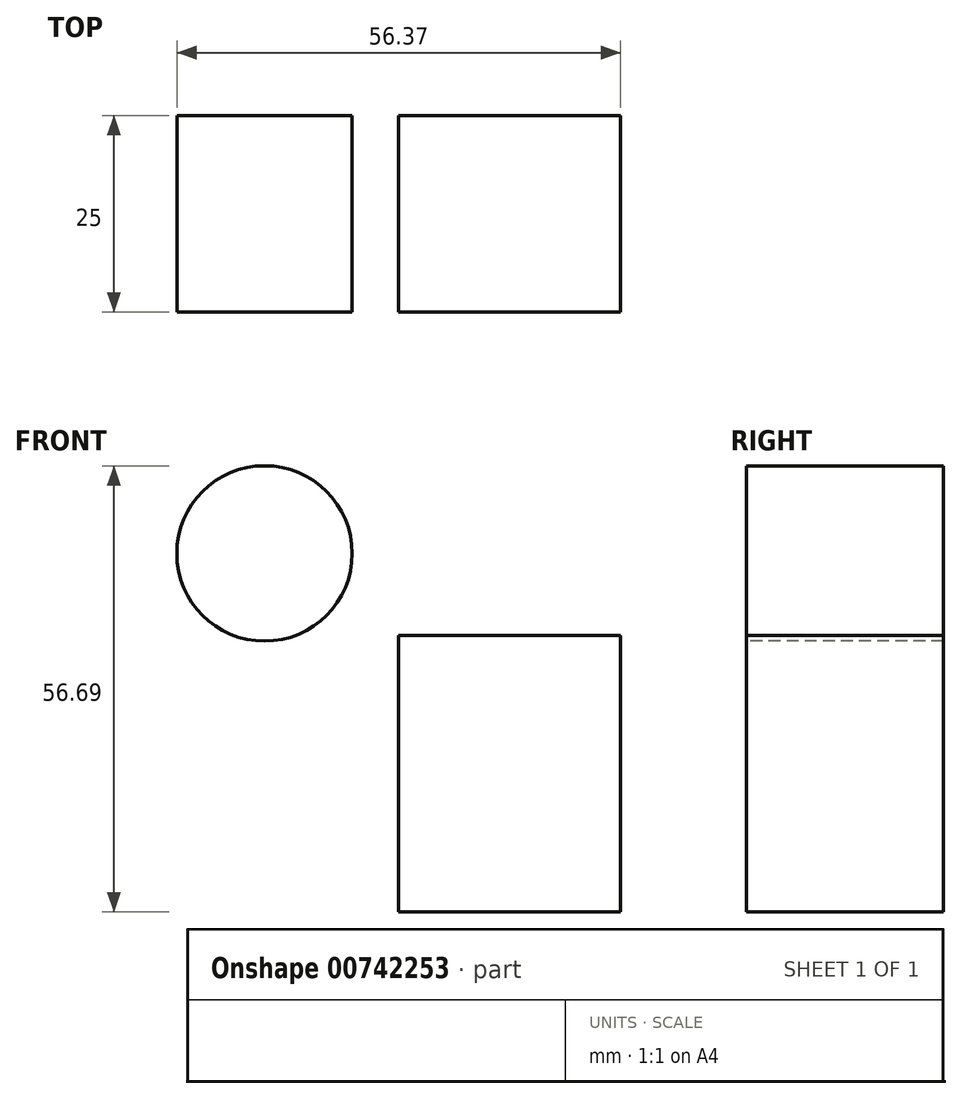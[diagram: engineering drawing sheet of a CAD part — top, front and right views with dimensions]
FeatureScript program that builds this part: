
annotation { "Feature Type Name" : "Feature", "Feature Type Description" : "" }
export const myFeature = defineFeature(function(context is Context, id is Id, definition is map)
    precondition{}
    {
        {
            var Q0;
            Q0=qCreatedBy(makeId("Front.planeOp"),FACE);
            var sketch = newSketch(context, id + "F0", { "sketchPlane" : qUnion([Q0])});
            skLineSegment(sketch, "E0.bottom", {"start": v(34.98, 28.17) * mm, "end": v(63.2, 28.17) * mm});
            skLineSegment(sketch, "E0.top", {"start": v(34.98, -6.96) * mm, "end": v(63.2, -6.96) * mm});
            skLineSegment(sketch, "E0.left", {"start": v(34.98, 28.17) * mm, "end": v(34.98, -6.96) * mm});
            skLineSegment(sketch, "E0.right", {"start": v(63.2, 28.17) * mm, "end": v(63.2, -6.96) * mm});
            skSolve(sketch);
        }
        {
            var Q0;
            Q0=qCreatedBy(makeId("Front.planeOp"),FACE);
            var sketch = newSketch(context, id + "F1", { "sketchPlane" : qUnion([Q0])});
            skCircle(sketch, "E1", {"center": v(17.97, 38.6) * mm, "radius": 11.14 * mm});
            skSolve(sketch);
        }
        {
            var Q0;
            Q0=sQuery(id+"F1.wireOp",EDGE,"E1");
            var Q1;
            Q1=sQuery(id+"F0.wireOp",EDGE,"E0.bottom");
            var Q2;
            Q2=sQuery(id+"F0.wireOp",EDGE,"E0.right");
            var Q3;
            Q3=sQuery(id+"F0.wireOp",EDGE,"E0.left");
            var Q4;
            Q4=sQuery(id+"F0.wireOp",EDGE,"E0.top");
            extrude(context, id + "F2", {"bodyType" : ToolBodyType.SURFACE, "surfaceEntities" : qUnion([Q0, Q1, Q2, Q3, Q4]), "depth" : 25 * mm, "offsetDistance" : 25 * mm});
        }
    });
